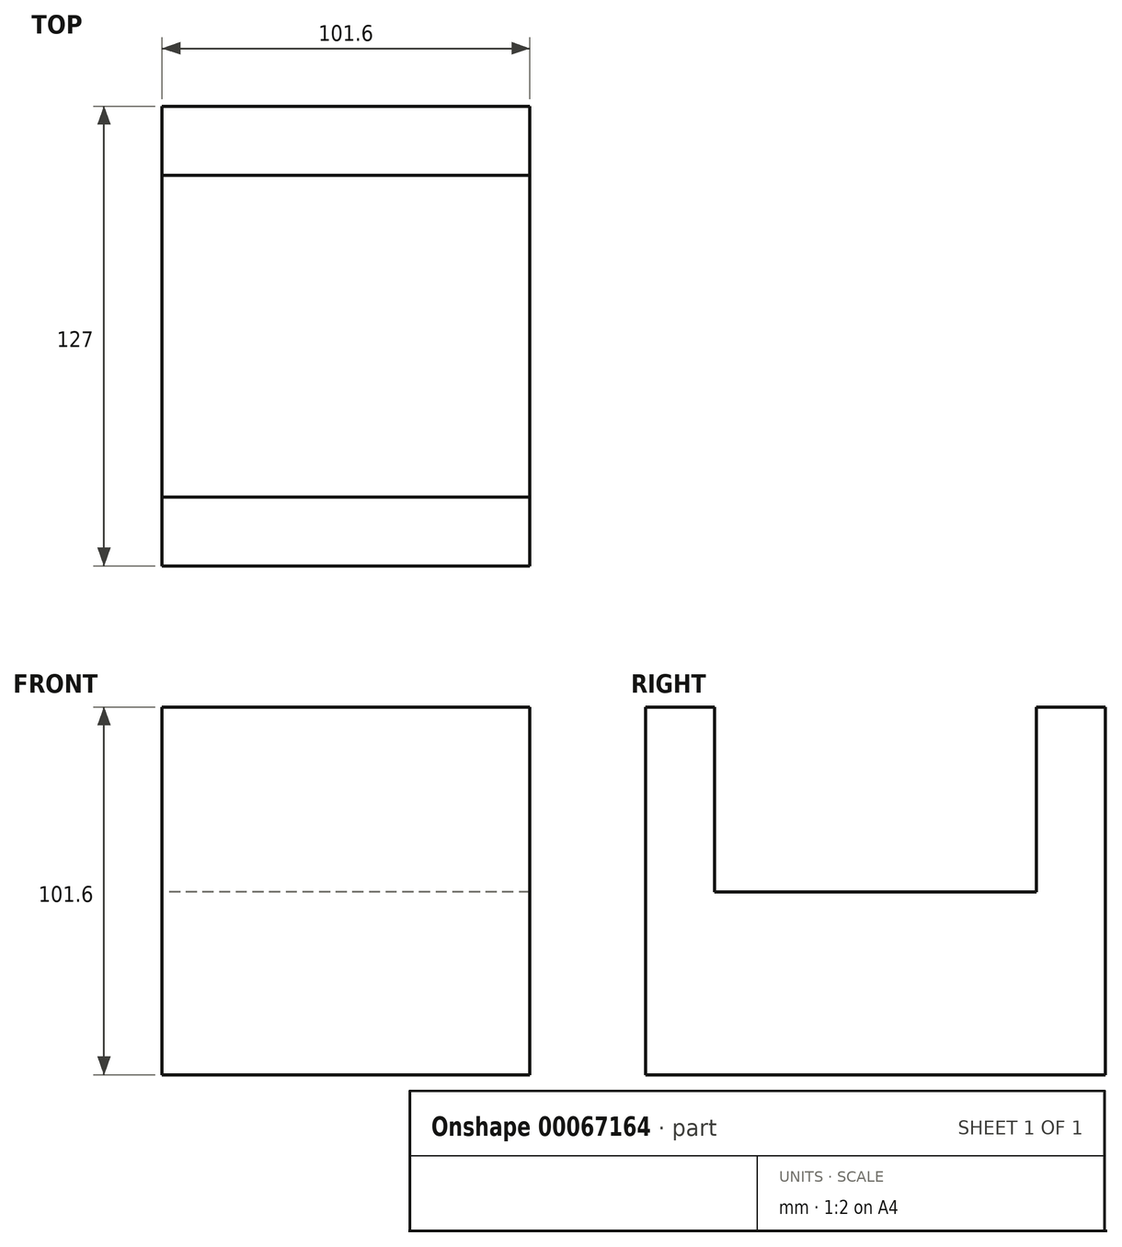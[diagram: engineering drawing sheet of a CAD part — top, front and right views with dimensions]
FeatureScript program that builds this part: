
annotation { "Feature Type Name" : "Feature", "Feature Type Description" : "" }
export const myFeature = defineFeature(function(context is Context, id is Id, definition is map)
    precondition{}
    {
        {
            var Q0;
            Q0=qCreatedBy(makeId("Front.planeOp"),FACE);
            var sketch = newSketch(context, id + "F0", { "sketchPlane" : qUnion([Q0])});
            skLineSegment(sketch, "E0.bottom", {"start": v(-50.55, 51.1) * mm, "end": v(51.05, 51.1) * mm});
            skLineSegment(sketch, "E0.top", {"start": v(-50.55, -50.5) * mm, "end": v(51.05, -50.5) * mm});
            skLineSegment(sketch, "E0.left", {"start": v(-50.55, 51.1) * mm, "end": v(-50.55, -50.5) * mm});
            skLineSegment(sketch, "E0.right", {"start": v(51.05, 51.1) * mm, "end": v(51.05, -50.5) * mm});
            skSolve(sketch);
        }
        {
            var Q0;
            Q0=makeQuery(id+"F0.imprint","IMPRINT",FACE,{"disambiguationData":[TD([[makeQuery(id+"F0.imprint","IMPRINT",EDGE,{"derivedFrom":sQuery(id+"F0.wireOp",EDGE,"E0.bottom")}),-1.0]])]});
            extrude(context, id + "F1", {"entities" : qUnion([Q0]), "depth" : 63.5 * mm, "hasSecondDirection" : true, "secondDirectionOppositeDirection" : true, "secondDirectionDepth" : 63.5 * mm});
        }
        {
            var Q0;
            Q0=qCreatedBy(makeId("Top.planeOp"),FACE);
            var sketch = newSketch(context, id + "F2", { "sketchPlane" : qUnion([Q0])});
            skLineSegment(sketch, "E1.bottom", {"start": v(51.05, 44.45) * mm, "end": v(-50.55, 44.45) * mm});
            skLineSegment(sketch, "E1.top", {"start": v(51.05, -44.45) * mm, "end": v(-50.55, -44.45) * mm});
            skLineSegment(sketch, "E1.left", {"start": v(51.05, 44.45) * mm, "end": v(51.05, -44.45) * mm});
            skLineSegment(sketch, "E1.right", {"start": v(-50.55, 44.45) * mm, "end": v(-50.55, -44.45) * mm});
            skSolve(sketch);
        }
        {
            var Q0;
            Q0 = qSketchRegion(id + "F2", true);
            extrude(context, id + "F3", {"entities" : qUnion([Q0]), "operationType" : NewBodyOperationType.REMOVE, "depth" : 81.22 * mm});
        }
    });
